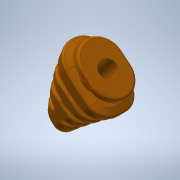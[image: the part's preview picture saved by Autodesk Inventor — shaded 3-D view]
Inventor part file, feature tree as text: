
AUTODESK INVENTOR PART (.ipt)
format: ipt  version: 2020 (Build 240168000, 168)  size: 9,414,144 bytes
history: native  units: in
note: dims shown in document units (in); Inventor stores cm internally (conversion verified against a paired STEP export)
features: fillet x15, sketch x13, extrude x8, delete_face x5, other x3, sweep x2, mirror x2, draft x1, boolean_combine x1, chamfer x1, plane x1
ambient origin geometry x8: Origin, YZ Plane, XZ Plane, XY Plane, X Axis, Y Axis, Z Axis, Center Point
bodies: Solid5 (feature_tree), Solid6 (feature_tree)
feature tree (52):
  other  "Part1b1.ipt"
  extrude  "Extrusion1"  Depth=1.1in
  sketch  "Sketch3-<F>"  dims[d7=0.78in d8=1.1in]
  sketch  "Sketch6-<F>"  dims[d10=1.0in d13=2.75in d14=0.975in d15=0.26in d16=0.405in d17=0.725in]
  sketch  "3D Sketch2"
  sweep  "Sweep3"
  delete_face  "Delete Face22"
  delete_face  "Delete Face23"
  draft  "FaceDraft1"
  mirror  "Mirror2"
  fillet  "Fillet12"  Radius=0.975in
  fillet  "Fillet13"  Radius=0.26in
  delete_face  "Delete Face24"
  delete_face  "Delete Face25"
  fillet  "Fillet14"  Radius=0.405in
  fillet  "Fillet15"  Radius=0.725in
  extrude  "Extrusion2"  Depth=2.695in
  fillet  "Fillet16"  Radius=0.268in
  fillet  "Fillet17"  Radius=0.12in
  fillet  "Fillet18"  Radius=0.3in
  boolean_combine  "Combine3"
  sketch  "Sketch10-<U>"  dims[d18=0.625in d19=2.695in d20=0.268in d21=0.12in d22=0.3in d23=-0.0687in]
  extrude  "Extrusion5"  Depth=1.035in
  extrude  "Extrusion6"  Depth=0.475in
  fillet  "Fillet19"  Radius=0.7in
  chamfer  "Chamfer2"  Distance=0.145in
  fillet  "Fillet20"  Radius=0.125in
  sweep  "Sweep4"
  delete_face  "Delete Face26"
  extrude  "Extrusion7"  Depth=0.0031in
  plane  "Work Plane3"
  extrude  "Extrusion10"  Depth=0.0031in
  mirror  "Mirror3"
  fillet  "Fillet25"  Radius=0.75in
  fillet  "Fillet28"  Radius=0.075in
  fillet  "Fillet26"  Radius=0.425in
  fillet  "Fillet29"  [1 undecoded]
  extrude  "Extrusion8"  Depth=0.0031in
  fillet  "Fillet23"  Radius=0.375in
  extrude  "Extrusion9"  Depth=0.0031in
  fillet  "Fillet24"  Radius=0.065in
  sketch  "Sketch2-<F>"  dims[d25=0.78in d26=1.035in]
  sketch  "Sketch7-<F>"  dims[d30=0.18in d31=0.475in d32=0.7in]
  other  "Solid1::Part1b1.ipt"
  other  "TaggingFeature1"
  sketch  "Sketch11-<F>"  dims[d33=0.975in]
  sketch  "Sketch14-<F>"  dims[d34=1.15in]
  sketch  "Sketch15-<F>"  dims[d35=1.3in]
  sketch  "Sketch16-<F>"  dims[d36=0.1in]
  sketch  "Sketch17-<F>"  dims[d37=0.112in]
  sketch  "Sketch18-<F>"  dims[d38=0.14in]
  sketch  "Sketch19-<F>"  dims[d39=0.15in d40=0.145in d41=0.125in d42=0.09in d53=0.0412in d54=0.35in d55=0.75in d56=0.075in d57=0.425in d58=0.0in d59=0.0in d60=0.4947in d61=0.375in d62=0.03in d63=0.065in d107=0.0687in d108=0.225in d109=0.5in d110=0.625in d111=0.3937in d112=0.64in d113=0.0in d114=0.45in d115=0.1969in d116=0.7in d117=0.1969in d118=0.475in d119=0.3in d120=0.55in d121=0.1722in d122=0.08in d123=0.06in d124=0.125in d125=0.3937in d126=0.08in d127=0.06in d128=0.125in d129=0.3937in d130=0.045in d131=0.09in d132=0.115in d133=0.2461in d134=0.045in d135=0.09in d136=0.115in d137=0.2541in d139=0.052in d140=0.06in d141=0.198in d142=0.2554in d143=0.0in d144=0.008in d145=0.02in d146=0.03in d147=0.143in d148=0.1755in d149=0.023in d150=0.1in d151=0.008in d154=0.03in d155=0.3937in d168=0.268in d169=1.512in d170=0.5in d171=0.7in d175=0.166in d176=0.0in d179=0.03in d180=0.06in d182=0.124in d183=0.124in d184=0.2505in d185=0.0375in d186=0.03in d187=0.0453in d188=0.0453in d189=0.0945in d190=0.0945in d191=0.0157in d192=0.0157in d193=0.05in d194=0.06in d195=0.05in d196=0.06in d197=0.0in d198=0.0in d199=0.0787in d200=0.0945in d204=0.04in d205=0.125in d206=0.1237in d207=0.01in d208=0.005in d209=1.875in d210=0.083in d211=0.0in d212=0.0in d215=0.015in d217=0.0481in d218=0.0481in d219=0.015in d220=0.015in d221=0.0481in d222=0.0481in d223=0.015in d225=0.0155in d226=0.0155in d227=0.015in d229=0.0481in d230=0.0481in d231=0.015in d233=0.0481in d234=0.0481in d235=0.015in d237=0.015in d239=0.0481in d240=0.0481in d241=0.0481in d242=0.0481in d243=0.3848in d247=0.015in d249=0.015in d250=0.481in d251=0.075in d252=0.4947in d253=0.07in d254=0.4466in d258=0.1066in d259=0.0in d262=0.02in d263=0.02in d264=0.0in d265=0.01in d266=0.15in d267=0.025in d268=0.05in d269=0.0in d270=0.005in d271=-0.11in d272=0.0354in d273=0.0in d274=0.015in d275=0.01in d277=0.1575in d278=0.189in d279=0.248in d280=0.323in d281=0.1575in d282=0.0059in d283=0.0031in]
note: 1 required parameter value undecoded (feature->parameter linkage not recoverable at this tier; creation-order binding heuristic only, values carry confidence <= 0.55)
